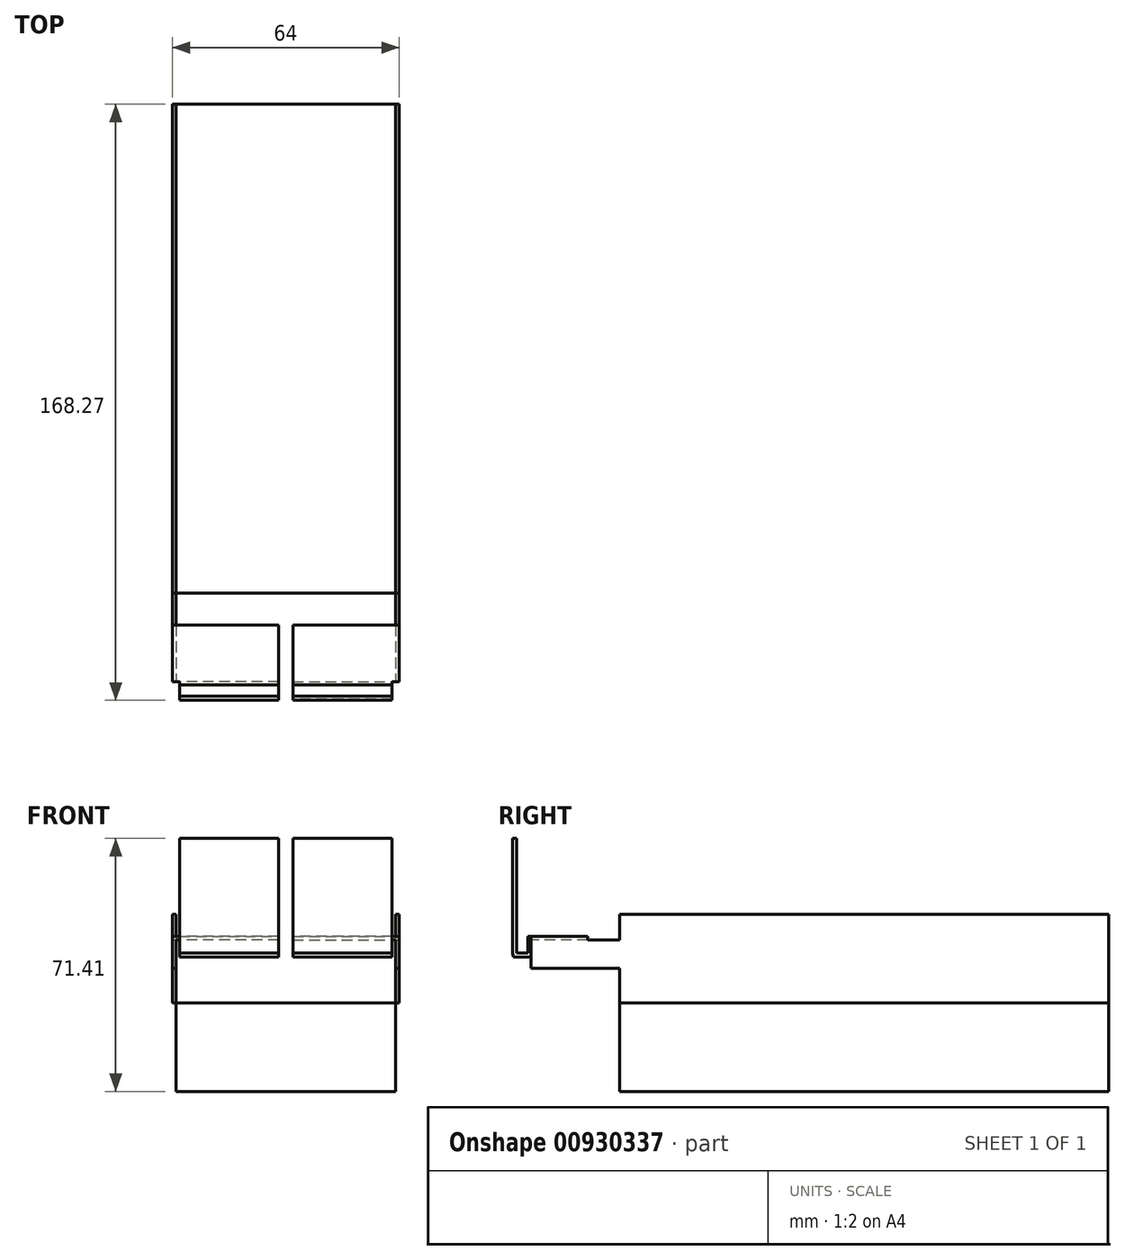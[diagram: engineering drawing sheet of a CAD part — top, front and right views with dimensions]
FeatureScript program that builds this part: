
annotation { "Feature Type Name" : "Feature", "Feature Type Description" : "" }
export const myFeature = defineFeature(function(context is Context, id is Id, definition is map)
    precondition{}
    {
        {
            var Q0;
            Q0=qCreatedBy(makeId("Top.planeOp"),FACE);
            var sketch = newSketch(context, id + "F0", { "sketchPlane" : qUnion([Q0])});
            skLineSegment(sketch, "E0.bottom", {"start": v(31, 69) * mm, "end": v(-31, 69) * mm});
            skLineSegment(sketch, "E0.top", {"start": v(31, -69) * mm, "end": v(-31, -69) * mm});
            skLineSegment(sketch, "E0.left", {"start": v(31, 69) * mm, "end": v(31, -69) * mm});
            skLineSegment(sketch, "E0.right", {"start": v(-31, 69) * mm, "end": v(-31, -69) * mm});
            skPoint(sketch, "E0.middle", {"position": v(0, 0) * mm});
            skSolve(sketch);
        }
        {
            var Q0;
            Q0 = qSketchRegion(id + "F0", true);
            extrude(context, id + "F1", {"entities" : qUnion([Q0]), "depth" : 25 * mm, "offsetDistance" : 25 * mm});
        }
        {
            var Q0;
            Q0=makeQuery(id+"F1.opExtrude","CAP_FACE",FACE,{"disambiguationData":[OSD([sQuery(id+"F0.wireOp",EDGE,"E0.bottom"),sQuery(id+"F0.wireOp",EDGE,"E0.top"),sQuery(id+"F0.wireOp",EDGE,"E0.left"),sQuery(id+"F0.wireOp",EDGE,"E0.right")])],"isStart":false});
            var sketch = newSketch(context, id + "F2", { "sketchPlane" : qUnion([Q0])});
            skLineSegment(sketch, "E1.bottom", {"start": v(-32, 69) * mm, "end": v(-31, 69) * mm});
            skLineSegment(sketch, "E1.top", {"start": v(-32, -69) * mm, "end": v(-31, -69) * mm});
            skLineSegment(sketch, "E1.left", {"start": v(-32, 69) * mm, "end": v(-32, -69) * mm});
            skLineSegment(sketch, "E1.right", {"start": v(-31, 69) * mm, "end": v(-31, -69) * mm});
            skPoint(sketch, "E1.middle", {"position": v(-31.5, 0) * mm});
            skLineSegment(sketch, "E2.MirrorCS", {"start": v(32, 69) * mm, "end": v(31, 69) * mm});
            skLineSegment(sketch, "E3.MirrorCS", {"start": v(32, -69) * mm, "end": v(31, -69) * mm});
            skLineSegment(sketch, "E4.MirrorCS", {"start": v(31, 69) * mm, "end": v(31, -69) * mm});
            skLineSegment(sketch, "E5.MirrorCS", {"start": v(32, 69) * mm, "end": v(32, -69) * mm});
            skPoint(sketch, "E6.MirrorP", {"position": v(31.5, 0) * mm});
            skSolve(sketch);
        }
        {
            var Q0;
            Q0=makeQuery(id+"F2.imprint","IMPRINT",FACE,{"disambiguationData":[TD([[makeQuery(id+"F2.imprint","IMPRINT",EDGE,{"derivedFrom":sQuery(id+"F2.wireOp",EDGE,"E1.bottom")}),-1.0]])]});
            var Q1;
            Q1=makeQuery(id+"F2.imprint","IMPRINT",FACE,{"disambiguationData":[TD([[makeQuery(id+"F2.imprint","IMPRINT",EDGE,{"derivedFrom":sQuery(id+"F2.wireOp",EDGE,"E2.MirrorCS")}),1.0]])]});
            extrude(context, id + "F3", {"entities" : qUnion([Q0, Q1]), "depth" : 25 * mm, "offsetDistance" : 25 * mm});
        }
        {
            var Q0;
            Q0=makeQuery(id+"F3.opExtrude","SWEPT_FACE",FACE,{"disambiguationData":[OSD([sQuery(id+"F2.wireOp",EDGE,"E1.left")])]});
            var sketch = newSketch(context, id + "F4", { "sketchPlane" : qUnion([Q0])});
            skSolve(sketch);
        }
        {
            var Q0;
            {var subQ0=sQuery(id+"F2.wireOp",EDGE,"E1.left");Q0=makeQuery(id+"F4.imprint","IMPRINT",FACE,{"disambiguationData":[TD([[makeQuery(id+"F4.imprint","IMPRINT",EDGE,{"derivedFrom":makeQuery(id+"F3.opExtrude","CAP_EDGE",EDGE,{"disambiguationData":[OSD([subQ0])],"isStart":true})}),1.0]])]});}
            var sketch = newSketch(context, id + "F5", { "sketchPlane" : qUnion([Q0])});
            skLineSegment(sketch, "E7.bottom", {"start": v(69, 42.72) * mm, "end": v(94, 42.72) * mm});
            skLineSegment(sketch, "E7.top", {"start": v(69, 34.72) * mm, "end": v(94, 34.72) * mm});
            skLineSegment(sketch, "E7.left", {"start": v(69, 42.72) * mm, "end": v(69, 34.72) * mm});
            skLineSegment(sketch, "E7.right", {"start": v(94, 42.72) * mm, "end": v(94, 34.72) * mm});
            skPoint(sketch, "E7.middle", {"position": v(81.5, 38.72) * mm});
            skSolve(sketch);
        }
        {
            var Q0;
            Q0 = qSketchRegion(id + "F5", true);
            var Q1;
            Q1=makeQuery(id+"F3.opExtrude","SWEPT_FACE",FACE,{"disambiguationData":[OSD([sQuery(id+"F2.wireOp",EDGE,"E1.right")])]});
            extrude(context, id + "F6", {"entities" : qUnion([Q0]), "operationType" : NewBodyOperationType.ADD, "endBound" : BoundingType.UP_TO_SURFACE, "oppositeDirection" : true, "depth" : 25 * mm, "endBoundEntityFace" : qUnion([Q1]), "offsetDistance" : 25 * mm});
        }
        {
            var Q0;
            Q0=makeQuery(id+"F6.boolean.opBoolean","MERGE",FACE,{"derivedFrom":[makeQuery(id+"F3.opExtrude","SWEPT_FACE",FACE,{"disambiguationData":[OSD([sQuery(id+"F2.wireOp",EDGE,"E1.left")])]}),makeQuery(id+"F6.opExtrude","CAP_FACE",FACE,{"disambiguationData":[OSD([sQuery(id+"F5.wireOp",EDGE,"E7.bottom"),sQuery(id+"F5.wireOp",EDGE,"E7.top"),sQuery(id+"F5.wireOp",EDGE,"E7.left"),sQuery(id+"F5.wireOp",EDGE,"E7.right")])],"isStart":true})]});
            var sketch = newSketch(context, id + "F7", { "sketchPlane" : qUnion([Q0])});
            skLineSegment(sketch, "E8.bottom", {"start": v(94, 42.72) * mm, "end": v(78, 42.72) * mm});
            skLineSegment(sketch, "E8.top", {"start": v(94, 43.72) * mm, "end": v(78, 43.72) * mm});
            skLineSegment(sketch, "E8.left", {"start": v(94, 42.72) * mm, "end": v(94, 43.72) * mm});
            skLineSegment(sketch, "E8.right", {"start": v(78, 42.72) * mm, "end": v(78, 43.72) * mm});
            skSolve(sketch);
        }
        {
            var Q0;
            Q0 = qSketchRegion(id + "F7", true);
            extrude(context, id + "F8", {"entities" : qUnion([Q0]), "operationType" : NewBodyOperationType.ADD, "oppositeDirection" : true, "depth" : 30 * mm, "offsetDistance" : 25 * mm});
        }
        {
            var Q0;
            Q0=makeQuery(id+"F8.opExtrude","CAP_FACE",FACE,{"disambiguationData":[OSD([sQuery(id+"F7.wireOp",EDGE,"E8.bottom"),sQuery(id+"F7.wireOp",EDGE,"E8.top"),sQuery(id+"F7.wireOp",EDGE,"E8.left"),sQuery(id+"F7.wireOp",EDGE,"E8.right")])],"isStart":false});
            var sketch = newSketch(context, id + "F9", { "sketchPlane" : qUnion([Q0])});
            skLineSegment(sketch, "E9.bottom", {"start": v(-94, 43.72) * mm, "end": v(-94.97, 43.72) * mm});
            skLineSegment(sketch, "E9.top", {"start": v(-94, 37.98) * mm, "end": v(-94.97, 37.98) * mm});
            skLineSegment(sketch, "E9.left", {"start": v(-94, 43.72) * mm, "end": v(-94, 37.98) * mm});
            skLineSegment(sketch, "E9.right", {"start": v(-94.97, 43.72) * mm, "end": v(-94.97, 39.01) * mm});
            skLineSegment(sketch, "E10.bottom", {"start": v(-94.97, 37.98) * mm, "end": v(-99, 37.98) * mm});
            skLineSegment(sketch, "E10.top", {"start": v(-94.97, 39.01) * mm, "end": v(-98.14, 39.01) * mm});
            skLineSegment(sketch, "E10.right", {"start": v(-99, 37.98) * mm, "end": v(-99.27, 39.01) * mm});
            skLineSegment(sketch, "E11.top", {"start": v(-99.27, 71.4) * mm, "end": v(-98.14, 71.4) * mm});
            skLineSegment(sketch, "E11.left", {"start": v(-99.27, 39.01) * mm, "end": v(-99.27, 71.4) * mm});
            skLineSegment(sketch, "E11.right", {"start": v(-98.14, 39.01) * mm, "end": v(-98.14, 71.4) * mm});
            skSolve(sketch);
        }
        {
            var Q0;
            {var subQ0=sQuery(id+"F9.wireOp",EDGE,"E9.bottom");Q0=makeQuery(id+"F9.imprint","IMPRINT",FACE,{"disambiguationData":[TD([[makeQuery(id+"F9.imprint","IMPRINT",EDGE,{"derivedFrom":subQ0}),1.0]])]});}
            extrude(context, id + "F10", {"entities" : qUnion([Q0]), "operationType" : NewBodyOperationType.ADD, "oppositeDirection" : true, "depth" : 28 * mm, "offsetDistance" : 25 * mm});
        }
        {
            var Q0;
            Q0=makeQuery(id+"F3.opExtrude","SWEPT_BODY",BODY,{"disambiguationData":[OSD([sQuery(id+"F2.wireOp",EDGE,"E2.MirrorCS"),sQuery(id+"F2.wireOp",EDGE,"E3.MirrorCS"),sQuery(id+"F2.wireOp",EDGE,"E4.MirrorCS"),sQuery(id+"F2.wireOp",EDGE,"E5.MirrorCS")])]});
            deleteBodies(context, id + "F11", {"entities" : qUnion([Q0])});
        }
        {
            var Q0;
            Q0=makeQuery(id+"F3.opExtrude","SWEPT_BODY",BODY,{"disambiguationData":[OSD([sQuery(id+"F2.wireOp",EDGE,"E1.bottom"),sQuery(id+"F2.wireOp",EDGE,"E1.top"),sQuery(id+"F2.wireOp",EDGE,"E1.left"),sQuery(id+"F2.wireOp",EDGE,"E1.right")])]});
            var Q1;
            Q1=qCreatedBy(makeId("Right.planeOp"),FACE);
            mirror(context, id + "F12", {"entities" : qUnion([Q0]), "mirrorPlane" : qUnion([Q1])});
        }
    });
